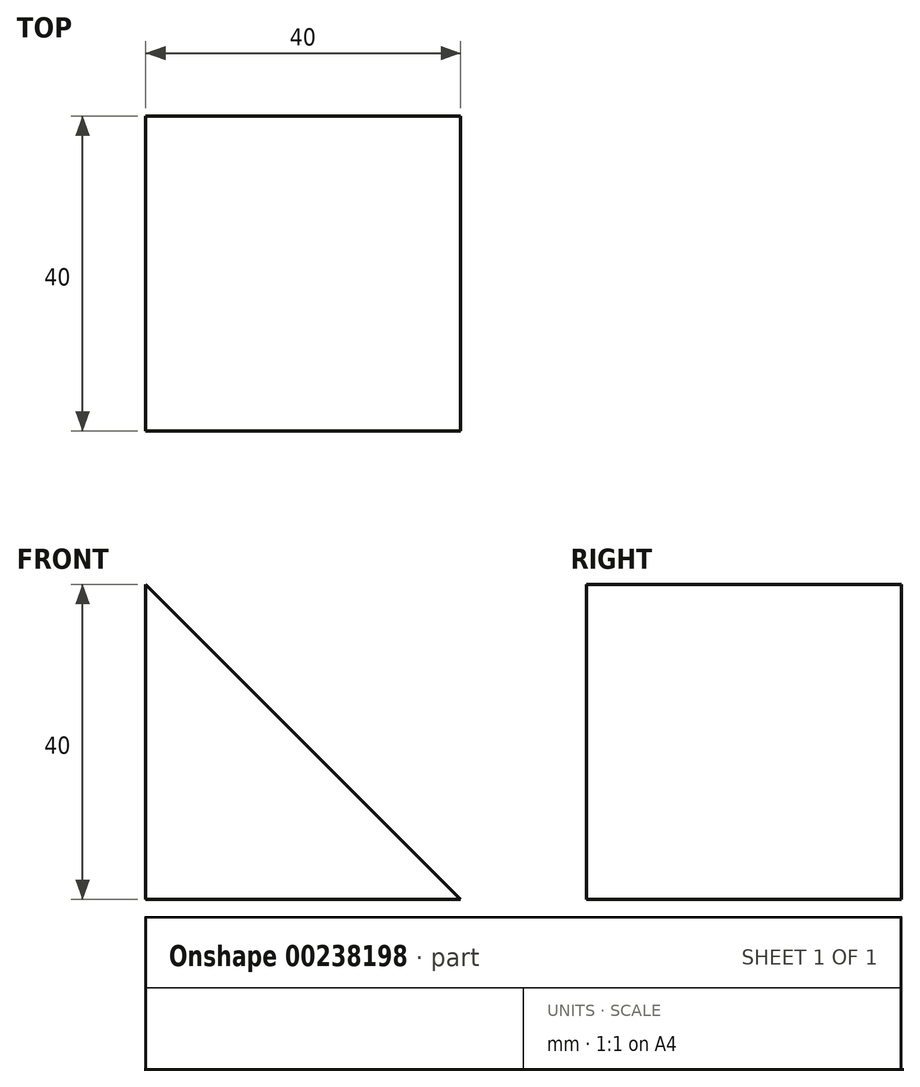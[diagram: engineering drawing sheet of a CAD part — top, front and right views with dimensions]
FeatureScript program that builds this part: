
annotation { "Feature Type Name" : "Feature", "Feature Type Description" : "" }
export const myFeature = defineFeature(function(context is Context, id is Id, definition is map)
    precondition{}
    {
        {
            var Q0;
            Q0=qCreatedBy(makeId("Top.planeOp"),FACE);
            var sketch = newSketch(context, id + "F0", { "sketchPlane" : qUnion([Q0])});
            skLineSegment(sketch, "E0.bottom", {"start": v(-20, -20) * mm, "end": v(20, -20) * mm});
            skLineSegment(sketch, "E0.top", {"start": v(-20, 20) * mm, "end": v(20, 20) * mm});
            skLineSegment(sketch, "E0.left", {"start": v(-20, -20) * mm, "end": v(-20, 20) * mm});
            skLineSegment(sketch, "E0.right", {"start": v(20, -20) * mm, "end": v(20, 20) * mm});
            skPoint(sketch, "E0.middle", {"position": v(0, 0) * mm});
            skSolve(sketch);
        }
        {
            var Q0;
            Q0=makeQuery(id+"F0.imprint","IMPRINT",FACE,{"disambiguationData":[TD([[makeQuery(id+"F0.imprint","IMPRINT",EDGE,{"derivedFrom":sQuery(id+"F0.wireOp",EDGE,"E0.bottom")}),1.0]])]});
            extrude(context, id + "F1", {"entities" : qUnion([Q0]), "depth" : 20 * mm, "hasSecondDirection" : true, "secondDirectionOppositeDirection" : true, "secondDirectionDepth" : 20 * mm});
        }
        {
            var Q0;
            Q0=makeQuery(id+"F1.opExtrude","CAP_EDGE",EDGE,{"disambiguationData":[OSD([sQuery(id+"F0.wireOp",EDGE,"E0.right")])],"isStart":false});
            chamfer(context, id + "F2", {"entities" : qUnion([Q0]), "width" : 40 * mm, "tangentPropagation" : true});
        }
    });
